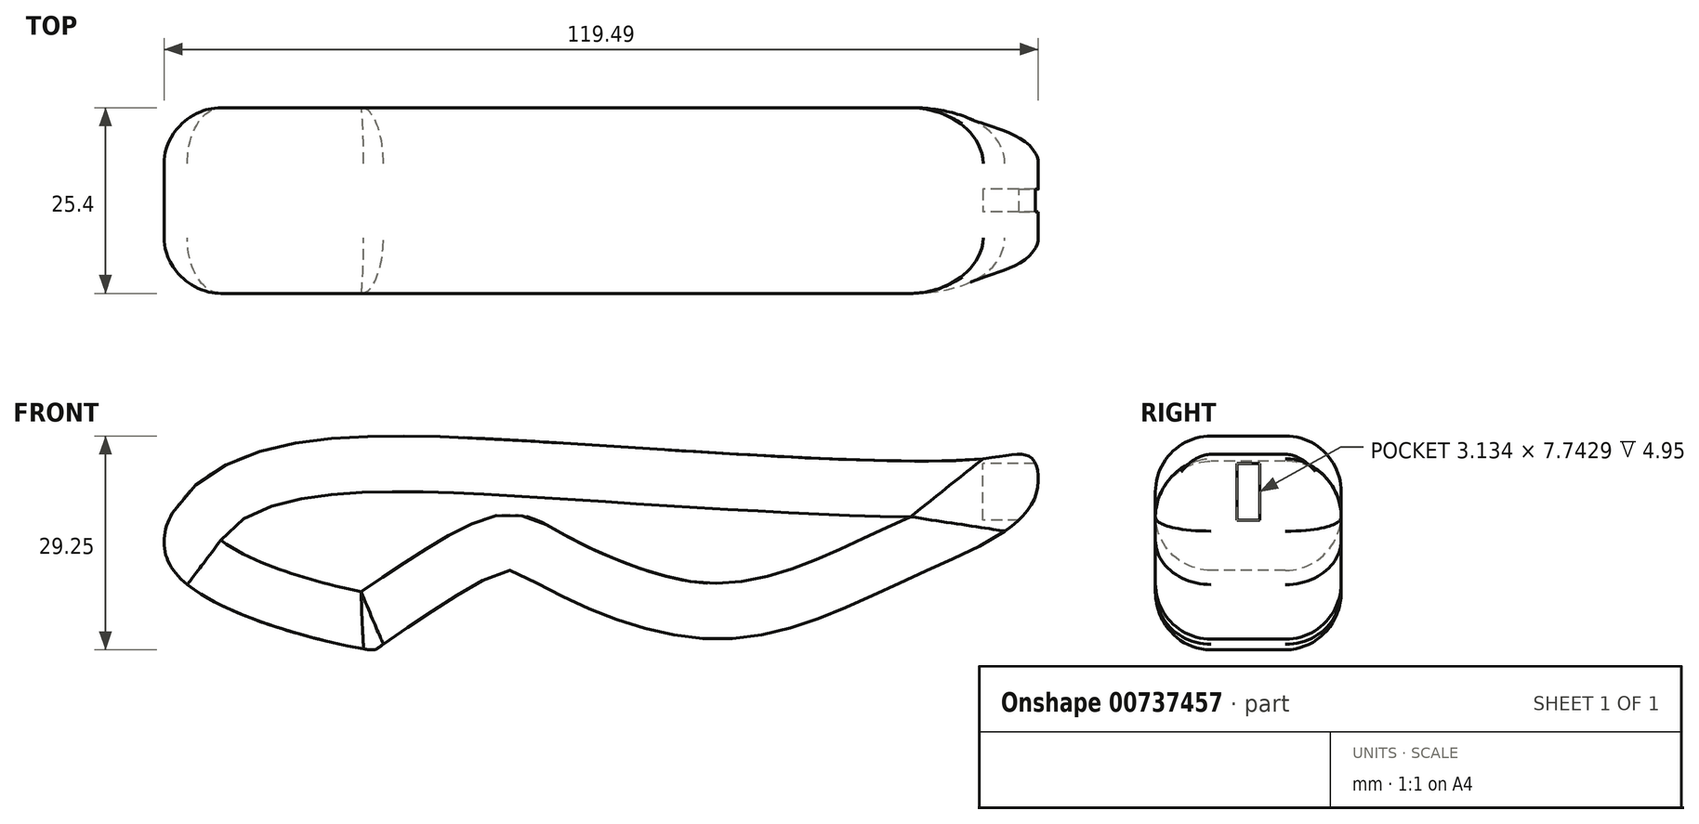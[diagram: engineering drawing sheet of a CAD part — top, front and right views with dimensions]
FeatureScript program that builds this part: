
annotation { "Feature Type Name" : "Feature", "Feature Type Description" : "" }
export const myFeature = defineFeature(function(context is Context, id is Id, definition is map)
    precondition{}
    {
        {
            var Q0;
            Q0=qCreatedBy(makeId("Front.planeOp"),FACE);
            var sketch = newSketch(context, id + "F0", { "sketchPlane" : qUnion([Q0])});
            skFitSpline(sketch, "E0", {"points": [v(0, 0) * mm, v(-60.38, 2.3) * mm, v(-105.36, -1.94) * mm, v(-110.52, -15.4) * mm, v(-84.16, -26.09) * mm, v(-82.13, -25.53) * mm, v(-66.1, -15.58) * mm, v(-62.59, -16.13) * mm, v(-38.44, -24.61) * mm, v(-9.5, -16.13) * mm, v(6.73, -6.18) * mm, v(6.73, 0) * mm, v(0, 0) * mm]});
            skSolve(sketch);
        }
        {
            var Q0;
            Q0 = qSketchRegion(id + "F0", true);
            extrude(context, id + "F1", {"entities" : qUnion([Q0]), "endBound" : BoundingType.SYMMETRIC, "depth" : 25.4 * mm, "offsetDistance" : 25.4 * mm});
        }
        {
            var Q0;
            Q0=makeQuery(id+"F1.opExtrude","CAP_EDGE",EDGE,{"disambiguationData":[OSD([sQuery(id+"F0.wireOp",EDGE,"E0")])],"isStart":false});
            var Q1;
            Q1=makeQuery(id+"F1.opExtrude","CAP_EDGE",EDGE,{"disambiguationData":[OSD([sQuery(id+"F0.wireOp",EDGE,"E0")])],"isStart":true});
            fillet(context, id + "F2", {"entities" : qUnion([Q0, Q1]), "radius" : 7.62 * mm, "tangentPropagation" : true, "allowEdgeOverflow" : false});
        }
        {
            var Q0;
            Q0=qCreatedBy(makeId("Right.planeOp"),FACE);
            var sketch = newSketch(context, id + "F3", { "sketchPlane" : qUnion([Q0])});
            skLineSegment(sketch, "E1.bottom", {"start": v(1.57, -8.39) * mm, "end": v(-1.57, -8.39) * mm});
            skLineSegment(sketch, "E1.top", {"start": v(1.57, -0.65) * mm, "end": v(-1.57, -0.65) * mm});
            skLineSegment(sketch, "E1.left", {"start": v(1.57, -8.39) * mm, "end": v(1.57, -0.65) * mm});
            skLineSegment(sketch, "E1.right", {"start": v(-1.57, -8.39) * mm, "end": v(-1.57, -0.65) * mm});
            skPoint(sketch, "E1.middle", {"position": v(0, -4.52) * mm});
            skSolve(sketch);
        }
        {
            var Q0;
            Q0 = qSketchRegion(id + "F3", true);
            extrude(context, id + "F4", {"entities" : qUnion([Q0]), "operationType" : NewBodyOperationType.REMOVE, "depth" : 25.4 * mm, "offsetDistance" : 25.4 * mm});
        }
    });
